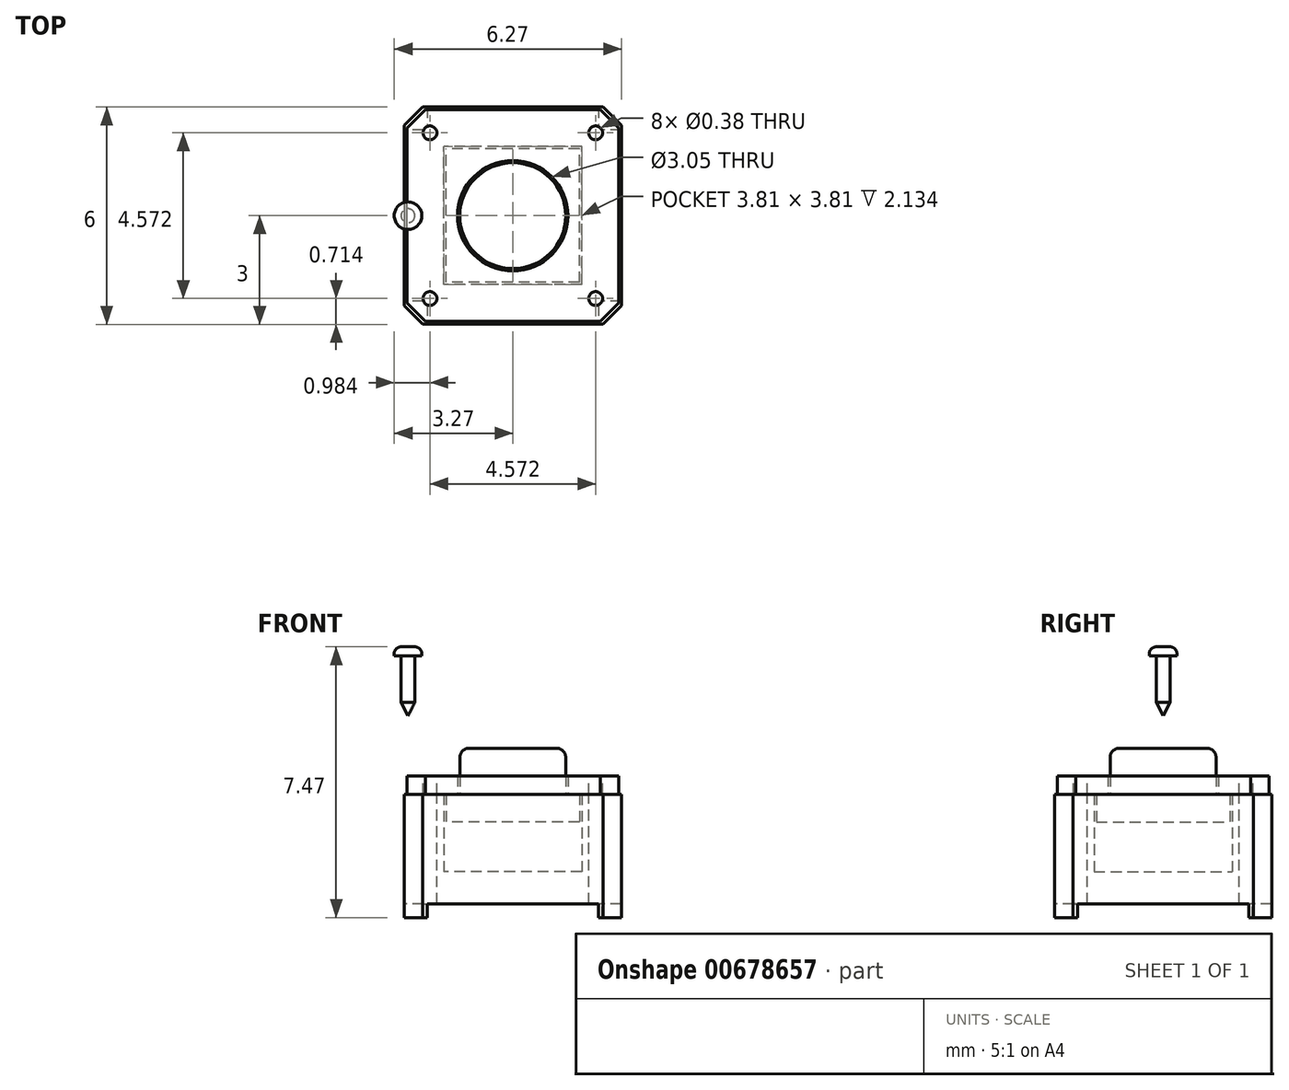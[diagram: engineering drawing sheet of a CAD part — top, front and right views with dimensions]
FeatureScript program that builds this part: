
annotation { "Feature Type Name" : "Feature", "Feature Type Description" : "" }
export const myFeature = defineFeature(function(context is Context, id is Id, definition is map)
    precondition{}
    {
        {
            var Q0;
            Q0=qCreatedBy(makeId("Top.planeOp"),FACE);
            var sketch = newSketch(context, id + "F0", { "sketchPlane" : qUnion([Q0])});
            skLineSegment(sketch, "E0.bottom", {"start": v(3, 3) * mm, "end": v(-3, 3) * mm});
            skLineSegment(sketch, "E0.top", {"start": v(3, -3) * mm, "end": v(-3, -3) * mm});
            skLineSegment(sketch, "E0.left", {"start": v(3, 3) * mm, "end": v(3, -3) * mm});
            skLineSegment(sketch, "E0.right", {"start": v(-3, 3) * mm, "end": v(-3, -3) * mm});
            skPoint(sketch, "E0.middle", {"position": v(0, 0) * mm});
            skLineSegment(sketch, "E1.bottom", {"start": v(1.9, -1.9) * mm, "end": v(-1.9, -1.9) * mm});
            skLineSegment(sketch, "E1.top", {"start": v(1.9, 1.9) * mm, "end": v(-1.9, 1.9) * mm});
            skLineSegment(sketch, "E1.left", {"start": v(1.9, -1.9) * mm, "end": v(1.9, 1.9) * mm});
            skLineSegment(sketch, "E1.right", {"start": v(-1.9, -1.9) * mm, "end": v(-1.9, 1.9) * mm});
            skSolve(sketch);
        }
        {
            var Q0;
            Q0 = qSketchRegion(id + "F0", true);
            extrude(context, id + "F1", {"entities" : qUnion([Q0]), "depth" : 3.4 * mm, "offsetDistance" : 25.4 * mm});
        }
        {
            var Q0;
            Q0=makeQuery(id+"F0.imprint","IMPRINT",FACE,{"disambiguationData":[TD([[makeQuery(id+"F0.imprint","IMPRINT",EDGE,{"derivedFrom":sQuery(id+"F0.wireOp",EDGE,"E1.bottom")}),-1.0]])]});
            extrude(context, id + "F2", {"entities" : qUnion([Q0]), "operationType" : NewBodyOperationType.ADD, "depth" : 1.27 * mm, "offsetDistance" : 25.4 * mm});
        }
        {
            var Q0;
            Q0=makeQuery(id+"F1.opExtrude","SWEPT_FACE",FACE,{"disambiguationData":[OSD([sQuery(id+"F0.wireOp",EDGE,"E0.top")])]});
            var sketch = newSketch(context, id + "F3", { "sketchPlane" : qUnion([Q0])});
            skLineSegment(sketch, "E2.bottom", {"start": v(-2.36, 0) * mm, "end": v(2.36, 0) * mm});
            skLineSegment(sketch, "E2.top", {"start": v(-2.36, 0.38) * mm, "end": v(2.36, 0.38) * mm});
            skLineSegment(sketch, "E2.left", {"start": v(-2.36, 0) * mm, "end": v(-2.36, 0.38) * mm});
            skLineSegment(sketch, "E2.right", {"start": v(2.36, 0) * mm, "end": v(2.36, 0.38) * mm});
            skSolve(sketch);
        }
        {
            var Q0;
            Q0 = qSketchRegion(id + "F3", true);
            var Q1;
            Q1=makeQuery(id+"F1.opExtrude","SWEPT_FACE",FACE,{"disambiguationData":[OSD([sQuery(id+"F0.wireOp",EDGE,"E0.bottom")])]});
            extrude(context, id + "F4", {"entities" : qUnion([Q0]), "operationType" : NewBodyOperationType.REMOVE, "endBound" : BoundingType.UP_TO_SURFACE, "oppositeDirection" : true, "depth" : 25.4 * mm, "endBoundEntityFace" : qUnion([Q1]), "offsetDistance" : 25.4 * mm});
        }
        {
            var Q0;
            Q0=makeQuery(id+"F1.opExtrude","SWEPT_EDGE",EDGE,{"disambiguationData":[OSD([sQuery(id+"F0.wireOp",EDGE,"E0.top"),sQuery(id+"F0.wireOp",EDGE,"E0.right")])]});
            var Q1;
            Q1=makeQuery(id+"F1.opExtrude","SWEPT_EDGE",EDGE,{"disambiguationData":[OSD([sQuery(id+"F0.wireOp",EDGE,"E0.bottom"),sQuery(id+"F0.wireOp",EDGE,"E0.right")])]});
            var Q2;
            Q2=makeQuery(id+"F1.opExtrude","SWEPT_EDGE",EDGE,{"disambiguationData":[OSD([sQuery(id+"F0.wireOp",EDGE,"E0.top"),sQuery(id+"F0.wireOp",EDGE,"E0.left")])]});
            var Q3;
            Q3=makeQuery(id+"F1.opExtrude","SWEPT_EDGE",EDGE,{"disambiguationData":[OSD([sQuery(id+"F0.wireOp",EDGE,"E0.bottom"),sQuery(id+"F0.wireOp",EDGE,"E0.left")])]});
            chamfer(context, id + "F5", {"entities" : qUnion([Q0, Q1, Q2, Q3]), "width" : 0.5 * mm, "tangentPropagation" : true});
        }
        {
            var Q0;
            Q0=makeQuery(id+"F1.opExtrude","CAP_FACE",FACE,{"disambiguationData":[OSD([sQuery(id+"F0.wireOp",EDGE,"E0.bottom"),sQuery(id+"F0.wireOp",EDGE,"E0.top"),sQuery(id+"F0.wireOp",EDGE,"E0.left"),sQuery(id+"F0.wireOp",EDGE,"E0.right"),sQuery(id+"F0.wireOp",EDGE,"E1.bottom"),sQuery(id+"F0.wireOp",EDGE,"E1.top"),sQuery(id+"F0.wireOp",EDGE,"E1.left"),sQuery(id+"F0.wireOp",EDGE,"E1.right")])],"isStart":false});
            var sketch = newSketch(context, id + "F6", { "sketchPlane" : qUnion([Q0])});
            skLineSegment(sketch, "E3.bottom", {"start": v(3, -2.92) * mm, "end": v(-2.92, -2.92) * mm});
            skLineSegment(sketch, "E3.top", {"start": v(2.92, 2.92) * mm, "end": v(-2.92, 2.92) * mm});
            skLineSegment(sketch, "E3.left", {"start": v(2.92, -2.92) * mm, "end": v(2.92, 2.92) * mm});
            skLineSegment(sketch, "E3.right", {"start": v(-2.92, -2.92) * mm, "end": v(-2.92, 2.92) * mm});
            skPoint(sketch, "E3.middle", {"position": v(0, 0) * mm});
            skCircle(sketch, "E4", {"center": v(0, 0) * mm, "radius": 1.52 * mm});
            skSolve(sketch);
        }
        {
            var Q0;
            Q0 = qSketchRegion(id + "F6", true);
            extrude(context, id + "F7", {"entities" : qUnion([Q0]), "depth" : 0.5 * mm, "offsetDistance" : 25.4 * mm});
        }
        {
            var Q0;
            Q0=makeQuery(id+"F7.opExtrude","SWEPT_EDGE",EDGE,{"disambiguationData":[OSD([sQuery(id+"F6.wireOp",EDGE,"E3.bottom"),sQuery(id+"F6.wireOp",EDGE,"E3.right")])]});
            var Q1;
            Q1=makeQuery(id+"F7.opExtrude","SWEPT_EDGE",EDGE,{"disambiguationData":[OSD([sQuery(id+"F6.wireOp",EDGE,"E3.top"),sQuery(id+"F6.wireOp",EDGE,"E3.right")])]});
            var Q2;
            Q2=makeQuery(id+"F7.opExtrude","SWEPT_EDGE",EDGE,{"disambiguationData":[OSD([sQuery(id+"F6.wireOp",EDGE,"E3.top"),sQuery(id+"F6.wireOp",EDGE,"E3.left")])]});
            var Q3;
            Q3=makeQuery(id+"F7.opExtrude","SWEPT_EDGE",EDGE,{"disambiguationData":[OSD([sQuery(id+"F6.wireOp",EDGE,"E3.bottom"),sQuery(id+"F6.wireOp",EDGE,"E3.left")])]});
            chamfer(context, id + "F8", {"entities" : qUnion([Q0, Q1, Q2, Q3]), "width" : 0.5 * mm, "tangentPropagation" : true});
        }
        {
            var Q0;
            Q0=makeQuery(id+"F1.opExtrude","SWEPT_FACE",FACE,{"disambiguationData":[OSD([sQuery(id+"F0.wireOp",EDGE,"E0.right")])]});
            var sketch = newSketch(context, id + "F9", { "sketchPlane" : qUnion([Q0])});
            skLineSegment(sketch, "E5.bottom", {"start": v(-2.36, 0) * mm, "end": v(2.36, 0) * mm});
            skLineSegment(sketch, "E5.top", {"start": v(-2.36, 0.38) * mm, "end": v(2.36, 0.38) * mm});
            skLineSegment(sketch, "E5.left", {"start": v(-2.36, 0) * mm, "end": v(-2.36, 0.38) * mm});
            skLineSegment(sketch, "E5.right", {"start": v(2.36, 0) * mm, "end": v(2.36, 0.38) * mm});
            skSolve(sketch);
        }
        {
            var Q0;
            Q0 = qSketchRegion(id + "F9", true);
            var Q1;
            Q1=makeQuery(id+"F1.opExtrude","SWEPT_FACE",FACE,{"disambiguationData":[OSD([sQuery(id+"F0.wireOp",EDGE,"E0.left")])]});
            extrude(context, id + "F10", {"entities" : qUnion([Q0]), "operationType" : NewBodyOperationType.REMOVE, "endBound" : BoundingType.UP_TO_SURFACE, "oppositeDirection" : true, "depth" : 25.4 * mm, "endBoundEntityFace" : qUnion([Q1]), "offsetDistance" : 25.4 * mm});
        }
        {
            var Q0;
            Q0=makeQuery(id+"F7.opExtrude","CAP_FACE",FACE,{"disambiguationData":[OSD([sQuery(id+"F6.wireOp",EDGE,"E3.bottom"),sQuery(id+"F6.wireOp",EDGE,"E3.top"),sQuery(id+"F6.wireOp",EDGE,"E3.left"),sQuery(id+"F6.wireOp",EDGE,"E3.right"),sQuery(id+"F6.wireOp",EDGE,"E4")])],"isStart":false});
            var sketch = newSketch(context, id + "F11", { "sketchPlane" : qUnion([Q0])});
            skCircle(sketch, "E6", {"center": v(-2.29, 2.29) * mm, "radius": 0.2 * mm});
            skLineSegment(sketch, "E7", {"start": v(0, 2.92) * mm, "end": v(0, -2.92) * mm, "construction": true});
            skLineSegment(sketch, "E8", {"start": v(2.92, 0) * mm, "end": v(-2.92, 0) * mm, "construction": true});
            skCircle(sketch, "E9.MirrorC", {"center": v(-2.29, -2.29) * mm, "radius": 0.2 * mm});
            skCircle(sketch, "E10.MirrorC", {"center": v(2.29, 2.29) * mm, "radius": 0.2 * mm});
            skCircle(sketch, "E11.MirrorC", {"center": v(2.29, -2.29) * mm, "radius": 0.2 * mm});
            skSolve(sketch);
        }
        {
            var Q0;
            Q0 = qSketchRegion(id + "F11", true);
            extrude(context, id + "F12", {"entities" : qUnion([Q0]), "operationType" : NewBodyOperationType.REMOVE, "oppositeDirection" : true, "depth" : 25.4 * mm, "offsetDistance" : 25.4 * mm});
        }
        {
            var Q0;
            Q0=makeQuery(id+"F1.opExtrude","CAP_FACE",FACE,{"disambiguationData":[OSD([sQuery(id+"F0.wireOp",EDGE,"E0.bottom"),sQuery(id+"F0.wireOp",EDGE,"E0.top"),sQuery(id+"F0.wireOp",EDGE,"E0.left"),sQuery(id+"F0.wireOp",EDGE,"E0.right"),sQuery(id+"F0.wireOp",EDGE,"E1.bottom"),sQuery(id+"F0.wireOp",EDGE,"E1.top"),sQuery(id+"F0.wireOp",EDGE,"E1.left"),sQuery(id+"F0.wireOp",EDGE,"E1.right")])],"isStart":false});
            cPlane(context, id + "F13", {"entities" : qUnion([Q0]), "cplaneType" : CPlaneType.OFFSET, "offset" : 0.76 * mm, "oppositeDirection" : true, "width" : 152.4 * mm, "height" : 152.4 * mm});
        }
        {
            var Q0;
            Q0=qCreatedBy(id+"F13.planeOp",FACE);
            var sketch = newSketch(context, id + "F14", { "sketchPlane" : qUnion([Q0])});
            skLineSegment(sketch, "E12.bottom", {"start": v(1.84, -1.84) * mm, "end": v(-1.84, -1.84) * mm});
            skLineSegment(sketch, "E12.top", {"start": v(1.84, 1.84) * mm, "end": v(-1.84, 1.84) * mm});
            skLineSegment(sketch, "E12.left", {"start": v(1.84, -1.84) * mm, "end": v(1.84, 1.84) * mm});
            skLineSegment(sketch, "E12.right", {"start": v(-1.84, -1.84) * mm, "end": v(-1.84, 1.84) * mm});
            skPoint(sketch, "E12.middle", {"position": v(0, 0) * mm});
            skCircle(sketch, "E13", {"center": v(0, 0) * mm, "radius": 1.46 * mm});
            skSolve(sketch);
        }
        {
            var Q0;
            Q0 = qSketchRegion(id + "F14", true);
            var Q1;
            Q1=makeQuery(id+"F1.opExtrude","CAP_FACE",FACE,{"disambiguationData":[OSD([sQuery(id+"F0.wireOp",EDGE,"E0.bottom"),sQuery(id+"F0.wireOp",EDGE,"E0.top"),sQuery(id+"F0.wireOp",EDGE,"E0.left"),sQuery(id+"F0.wireOp",EDGE,"E0.right"),sQuery(id+"F0.wireOp",EDGE,"E1.bottom"),sQuery(id+"F0.wireOp",EDGE,"E1.top"),sQuery(id+"F0.wireOp",EDGE,"E1.left"),sQuery(id+"F0.wireOp",EDGE,"E1.right")])],"isStart":false});
            extrude(context, id + "F15", {"entities" : qUnion([Q0]), "endBound" : BoundingType.UP_TO_SURFACE, "depth" : 25.4 * mm, "endBoundEntityFace" : qUnion([Q1]), "offsetDistance" : 25.4 * mm});
        }
        {
            var Q0;
            Q0=makeQuery(id+"F14.imprint","IMPRINT",FACE,{"disambiguationData":[TD([[makeQuery(id+"F14.imprint","IMPRINT",EDGE,{"derivedFrom":sQuery(id+"F14.wireOp",EDGE,"E13")}),1.0]])]});
            extrude(context, id + "F16", {"entities" : qUnion([Q0]), "operationType" : NewBodyOperationType.ADD, "depth" : 2.03 * mm, "offsetDistance" : 25.4 * mm});
        }
        {
            var Q0;
            Q0=makeQuery(id+"F16.opExtrude","CAP_FACE",FACE,{"disambiguationData":[OSD([sQuery(id+"F14.wireOp",EDGE,"E13")])],"isStart":false});
            fillet(context, id + "F17", {"entities" : qUnion([Q0]), "radius" : 0.25 * mm, "tangentPropagation" : true, "allowEdgeOverflow" : false});
        }
        {
            var Q0;
            Q0=qCreatedBy(makeId("Front.planeOp"),FACE);
            var sketch = newSketch(context, id + "F18", { "sketchPlane" : qUnion([Q0])});
            skLineSegment(sketch, "E14", {"start": v(-2.9, 9) * mm, "end": v(-2.9, 5.57) * mm, "construction": true});
            skLineSegment(sketch, "E15", {"start": v(-2.9, 5.57) * mm, "end": v(-3.08, 5.94) * mm});
            skLineSegment(sketch, "E16", {"start": v(-3.08, 5.94) * mm, "end": v(-3.08, 7.22) * mm});
            skLineSegment(sketch, "E17", {"start": v(-3.08, 7.22) * mm, "end": v(-3.27, 7.22) * mm});
            skLineSegment(sketch, "E18", {"start": v(-3.27, 7.22) * mm, "end": v(-3.27, 7.28) * mm});
            skLineSegment(sketch, "E19", {"start": v(-3.08, 7.47) * mm, "end": v(-2.9, 7.47) * mm});
            skPoint(sketch, "E20.visualSharp", {"position": v(-3.27, 7.47) * mm});
            skArc(sketch, "E20.filletArc", {"start": v(-3.08, 7.47) * mm, "mid": v(-3.22, 7.42) * mm, "end": v(-3.27, 7.28) * mm});
            skLineSegment(sketch, "E21", {"start": v(-2.9, 7.47) * mm, "end": v(-2.9, 5.57) * mm});
            skSolve(sketch);
        }
        {
            var Q0;
            Q0 = qSketchRegion(id + "F18", true);
            var Q1;
            Q1=sQuery(id+"F18.wireOp",EDGE,"E14");
            revolve(context, id + "F19", {"entities" : qUnion([Q0]), "axis" : qUnion([Q1]), "revolveType" : RevolveType.FULL});
        }
    });
